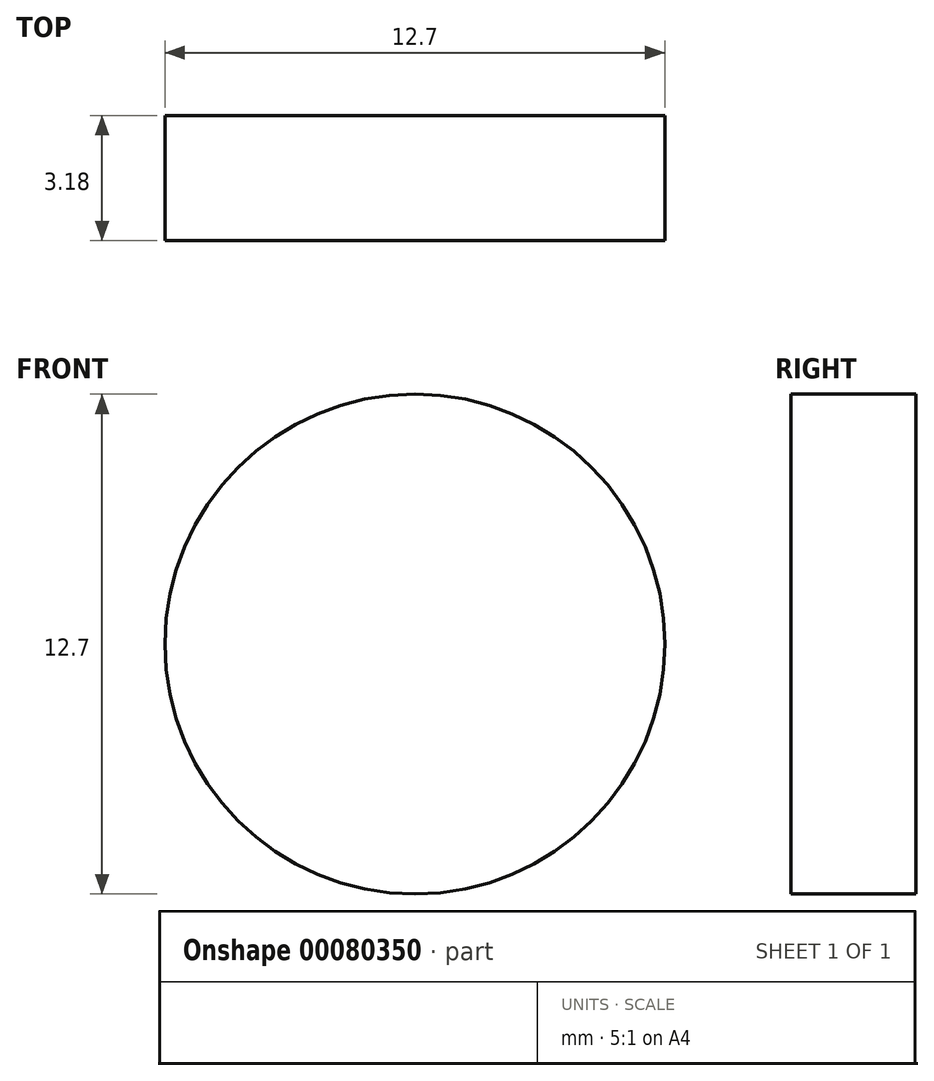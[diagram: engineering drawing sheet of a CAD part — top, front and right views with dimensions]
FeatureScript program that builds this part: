
annotation { "Feature Type Name" : "Feature", "Feature Type Description" : "" }
export const myFeature = defineFeature(function(context is Context, id is Id, definition is map)
    precondition{}
    {
        {
            var Q0;
            Q0=qCreatedBy(makeId("Front.planeOp"),FACE);
            var sketch = newSketch(context, id + "F0", { "sketchPlane" : qUnion([Q0])});
            skCircle(sketch, "E0", {"center": v(0, 0) * mm, "radius": 6.35 * mm});
            skSolve(sketch);
        }
        {
            var Q0;
            Q0=makeQuery(id+"F0.imprint","IMPRINT",FACE,{"disambiguationData":[TD([[makeQuery(id+"F0.imprint","IMPRINT",EDGE,{"derivedFrom":sQuery(id+"F0.wireOp",EDGE,"E0")}),1.0]])]});
            extrude(context, id + "F1", {"entities" : qUnion([Q0]), "endBound" : BoundingType.SYMMETRIC, "depth" : 3.17 * mm});
        }
    });
